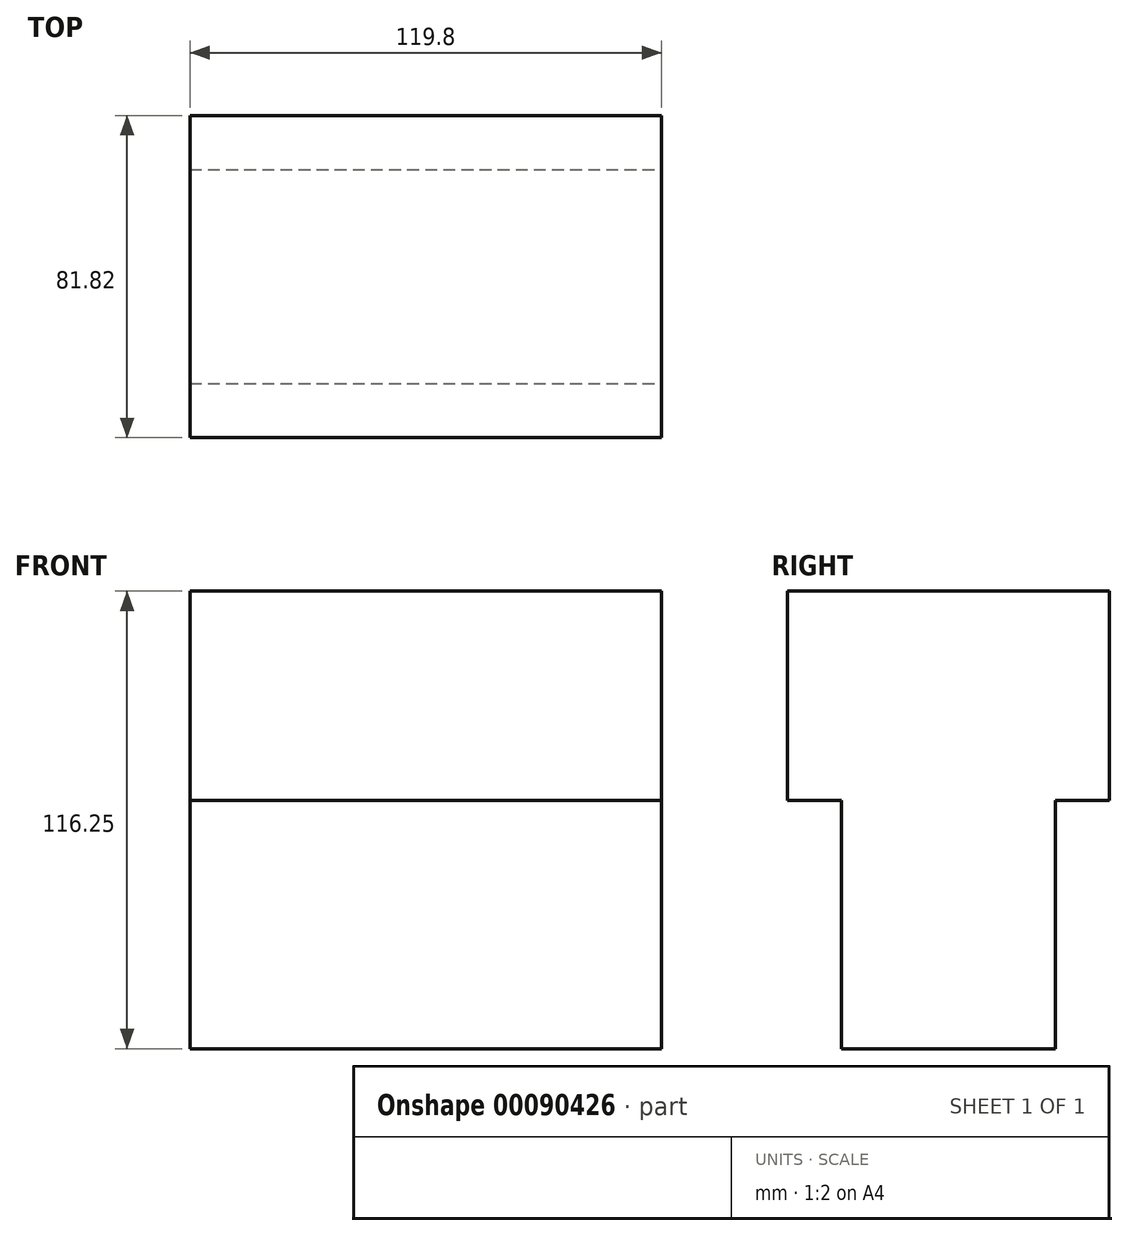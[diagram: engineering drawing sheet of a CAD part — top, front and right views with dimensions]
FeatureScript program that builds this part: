
annotation { "Feature Type Name" : "Feature", "Feature Type Description" : "" }
export const myFeature = defineFeature(function(context is Context, id is Id, definition is map)
    precondition{}
    {
        {
            var Q0;
            Q0=qCreatedBy(makeId("Top.planeOp"),FACE);
            var sketch = newSketch(context, id + "F0", { "sketchPlane" : qUnion([Q0])});
            skLineSegment(sketch, "E0.bottom", {"start": v(-59.9, -27.15) * mm, "end": v(59.9, -27.15) * mm});
            skLineSegment(sketch, "E0.top", {"start": v(-59.9, 27.15) * mm, "end": v(59.9, 27.15) * mm});
            skLineSegment(sketch, "E0.left", {"start": v(-59.9, -27.15) * mm, "end": v(-59.9, 27.15) * mm});
            skLineSegment(sketch, "E0.right", {"start": v(59.9, -27.15) * mm, "end": v(59.9, 27.15) * mm});
            skPoint(sketch, "E0.middle", {"position": v(0, 0) * mm});
            skSolve(sketch);
        }
        {
            var Q0;
            Q0=makeQuery(id+"F0.imprint","IMPRINT",FACE,{"disambiguationData":[TD([[makeQuery(id+"F0.imprint","IMPRINT",EDGE,{"derivedFrom":sQuery(id+"F0.wireOp",EDGE,"E0.bottom")}),1.0]])]});
            extrude(context, id + "F1", {"entities" : qUnion([Q0]), "depth" : 32.96 * mm});
        }
        {
            var Q0;
            Q0=makeQuery(id+"F1.opExtrude","CAP_FACE",FACE,{"disambiguationData":[OSD([sQuery(id+"F0.wireOp",EDGE,"E0.bottom"),sQuery(id+"F0.wireOp",EDGE,"E0.top"),sQuery(id+"F0.wireOp",EDGE,"E0.left"),sQuery(id+"F0.wireOp",EDGE,"E0.right")])],"isStart":true});
            extrude(context, id + "F2", {"entities" : qUnion([Q0]), "operationType" : NewBodyOperationType.ADD, "depth" : 30.1 * mm});
        }
        {
            var Q0;
            Q0=makeQuery(id+"F1.opExtrude","CAP_FACE",FACE,{"disambiguationData":[OSD([sQuery(id+"F0.wireOp",EDGE,"E0.bottom"),sQuery(id+"F0.wireOp",EDGE,"E0.top"),sQuery(id+"F0.wireOp",EDGE,"E0.left"),sQuery(id+"F0.wireOp",EDGE,"E0.right")])],"isStart":false});
            var sketch = newSketch(context, id + "F3", { "sketchPlane" : qUnion([Q0])});
            skLineSegment(sketch, "E1.bottom", {"start": v(-59.9, -40.91) * mm, "end": v(59.9, -40.91) * mm});
            skLineSegment(sketch, "E1.top", {"start": v(-59.9, 40.91) * mm, "end": v(59.9, 40.91) * mm});
            skLineSegment(sketch, "E1.left", {"start": v(-59.9, -40.91) * mm, "end": v(-59.9, 40.91) * mm});
            skLineSegment(sketch, "E1.right", {"start": v(59.9, -40.91) * mm, "end": v(59.9, 40.91) * mm});
            skPoint(sketch, "E1.middle", {"position": v(0, 0) * mm});
            skSolve(sketch);
        }
        {
            var Q0;
            Q0 = qSketchRegion(id + "F3", true);
            extrude(context, id + "F4", {"entities" : qUnion([Q0]), "operationType" : NewBodyOperationType.ADD, "depth" : 53.19 * mm});
        }
    });
